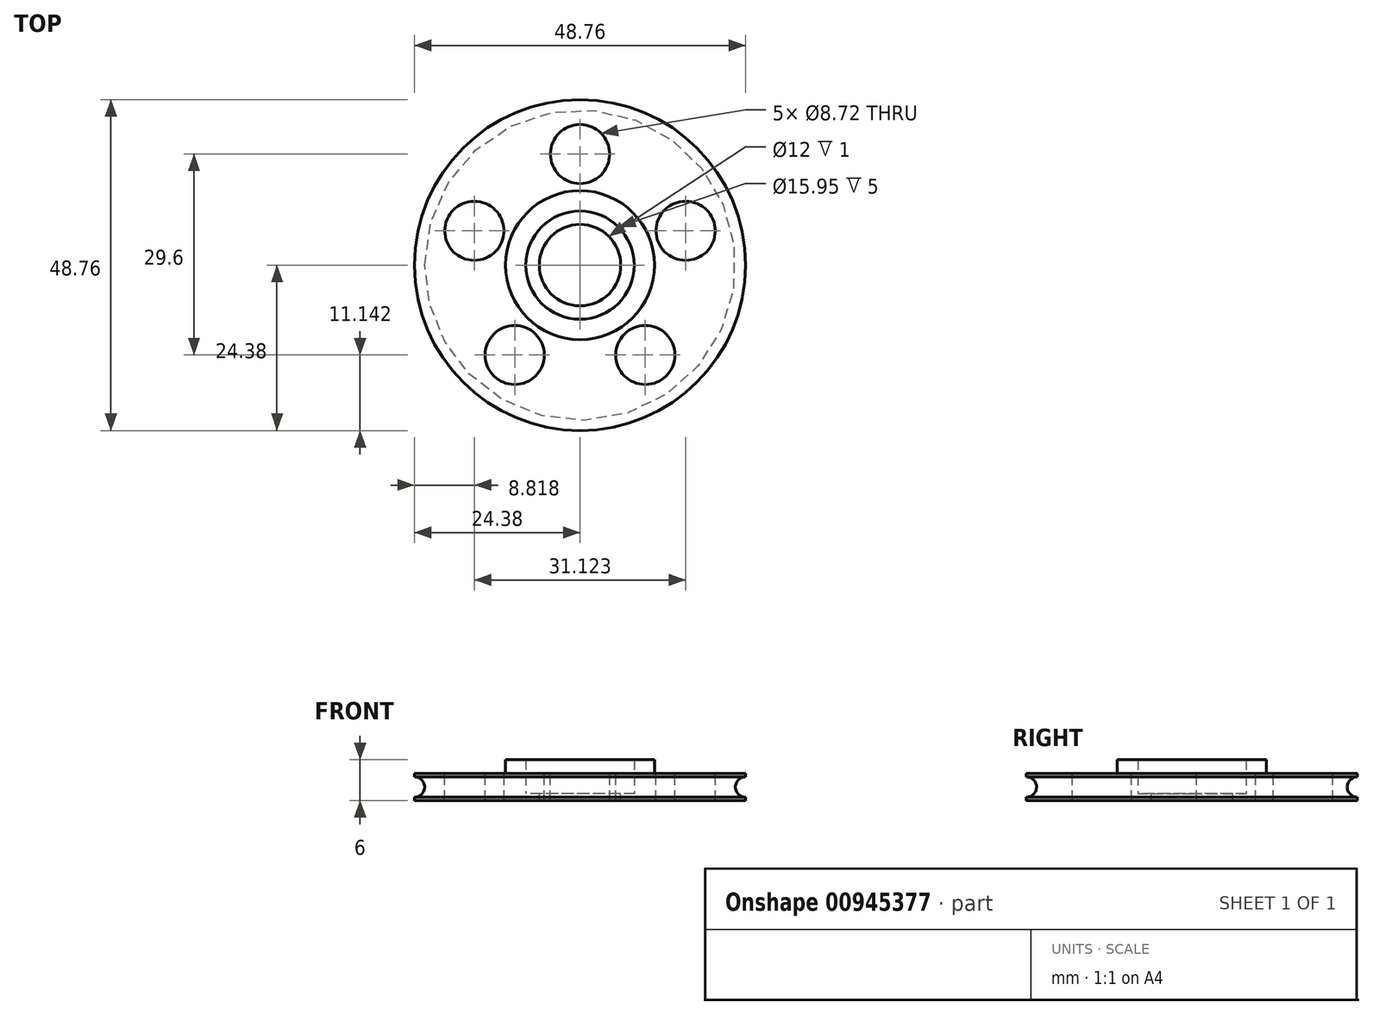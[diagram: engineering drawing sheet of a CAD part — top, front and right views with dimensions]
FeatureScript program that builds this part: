
annotation { "Feature Type Name" : "Feature", "Feature Type Description" : "" }
export const myFeature = defineFeature(function(context is Context, id is Id, definition is map)
    precondition{}
    {
        {
            var Q0;
            Q0=qCreatedBy(makeId("Top.planeOp"),FACE);
            var sketch = newSketch(context, id + "F0", { "sketchPlane" : qUnion([Q0])});
            skCircle(sketch, "E0", {"center": v(0, 0) * mm, "radius": 24.38 * mm});
            skSolve(sketch);
        }
        {
            var Q0;
            Q0=makeQuery(id+"F0.imprint","IMPRINT",FACE,{"disambiguationData":[TD([[makeQuery(id+"F0.imprint","IMPRINT",EDGE,{"derivedFrom":sQuery(id+"F0.wireOp",EDGE,"E0")}),1.0]])]});
            extrude(context, id + "F1", {"entities" : qUnion([Q0]), "depth" : 4 * mm, "offsetDistance" : 25.4 * mm});
        }
        {
            var Q0;
            Q0=makeQuery(id+"F1.opExtrude","CAP_FACE",FACE,{"disambiguationData":[OSD([sQuery(id+"F0.wireOp",EDGE,"E0"),sQuery(id+"F0.wireOp",EDGE,"n39IqKt5-bk1q-LU1x-fgod-8OyBNiFTd7FZ")])],"isStart":false});
            var sketch = newSketch(context, id + "F2", { "sketchPlane" : qUnion([Q0])});
            skCircle(sketch, "E1", {"center": v(0, 0) * mm, "radius": 7.97 * mm});
            skCircle(sketch, "E2.0", {"center": v(0, 0) * mm, "radius": 10.97 * mm});
            skSolve(sketch);
        }
        {
            var Q0;
            Q0=qSketchRegion(id+"F2",true);
            extrude(context, id + "F3", {"entities" : qUnion([Q0]), "operationType" : NewBodyOperationType.ADD, "depth" : 2 * mm, "offsetDistance" : 25.4 * mm});
        }
        {
            var Q0;
            Q0=makeQuery(id+"F3.boolean.opBoolean","SPLIT",FACE,{"disambiguationData":[TD([makeQuery(id+"F3.opExtrude","SWEPT_FACE",FACE,{"disambiguationData":[OSD([sQuery(id+"F2.wireOp",EDGE,"E1")])]})])],"derivedFrom":makeQuery(id+"F1.opExtrude","CAP_FACE",FACE,{"disambiguationData":[OSD([sQuery(id+"F0.wireOp",EDGE,"E0")])],"isStart":false})});
            var sketch = newSketch(context, id + "F4", { "sketchPlane" : qUnion([Q0])});
            skCircle(sketch, "E3", {"center": v(0, 0) * mm, "radius": 6 * mm});
            skSolve(sketch);
        }
        {
            var Q0;
            Q0=makeQuery(id+"F4.imprint","IMPRINT",FACE,{"disambiguationData":[TD([[makeQuery(id+"F4.imprint","IMPRINT",EDGE,{"derivedFrom":sQuery(id+"F4.wireOp",EDGE,"E3")}),1.0]])]});
            var Q1;
            Q1=makeQuery(id+"F4.imprint","IMPRINT",FACE,{"disambiguationData":[TD([[makeQuery(id+"F4.imprint","IMPRINT",EDGE,{"derivedFrom":makeQuery(id+"FgYK8jIepfClWtA_1.opExtrude","CAP_EDGE",EDGE,{"disambiguationData":[OSD([sQuery(id+"F8DXjnVyigKkjng_1.wireOp",EDGE,"EUjAMsCd-Zx2B-3j4q-cP5o-T3GrjTijNDqK")])],"isStart":false})}),1.0]])]});
            extrude(context, id + "F5", {"entities" : qUnion([Q0, Q1]), "operationType" : NewBodyOperationType.REMOVE, "oppositeDirection" : true, "depth" : 9 * mm, "offsetDistance" : 25.4 * mm});
        }
        {
            var Q0;
            Q0=qCreatedBy(makeId("Front.planeOp"),FACE);
            var sketch = newSketch(context, id + "F6", { "sketchPlane" : qUnion([Q0])});
            skCircle(sketch, "E4", {"center": v(-24.38, 2) * mm, "radius": 1.5 * mm});
            skLineSegment(sketch, "E5.bottom", {"start": v(-22.88, 0.65) * mm, "end": v(-25.02, 0.65) * mm});
            skLineSegment(sketch, "E5.top", {"start": v(-22.88, 3.35) * mm, "end": v(-25.02, 3.35) * mm});
            skLineSegment(sketch, "E5.left", {"start": v(-22.88, 0.65) * mm, "end": v(-22.88, 3.35) * mm});
            skLineSegment(sketch, "E5.right", {"start": v(-25.73, 1.35) * mm, "end": v(-25.73, 2.65) * mm});
            skLineSegment(sketch, "E6", {"start": v(0, 19.1) * mm, "end": v(0, -12.61) * mm, "construction": true});
            skLineSegment(sketch, "E7", {"start": v(-24.37, 3.35) * mm, "end": v(-22.88, 2) * mm});
            skLineSegment(sketch, "E8", {"start": v(-22.88, 2) * mm, "end": v(-24.38, 0.65) * mm});
            skLineSegment(sketch, "E9", {"start": v(-24.38, 0.65) * mm, "end": v(-24.37, 3.35) * mm});
            skSolve(sketch);
        }
        {
            var Q0;
            {var subQ0=sQuery(id+"F6.wireOp",EDGE,"E5.top");var subQ1=sQuery(id+"F6.wireOp",EDGE,"E4");var subQ2=makeQuery(id+"F6.imprint","INTERSECT",VERTEX,{"disambiguationData":[OD(0.0)],"derivedFrom":[subQ1,subQ0]});Q0=makeQuery(id+"F6.imprint","IMPRINT",FACE,{"disambiguationData":[TD([[makeQuery(id+"F6.imprint","IMPRINT",EDGE,{"disambiguationData":[TD([[subQ2,1.0]])],"derivedFrom":subQ1}),1.0]])]});}
            var Q1;
            {var subQ0=sQuery(id+"F6.wireOp",EDGE,"E5.bottom");var subQ1=sQuery(id+"F6.wireOp",EDGE,"E4");var subQ2=makeQuery(id+"F6.imprint","INTERSECT",VERTEX,{"disambiguationData":[OD(0.0)],"derivedFrom":[subQ1,subQ0]});Q1=makeQuery(id+"F6.imprint","IMPRINT",FACE,{"disambiguationData":[TD([[makeQuery(id+"F6.imprint","IMPRINT",EDGE,{"disambiguationData":[TD([[subQ2,-1.0]])],"derivedFrom":subQ1}),1.0]])]});}
            var Q2;
            {var subQ4=sQuery(id+"F6.wireOp",EDGE,"E5.right");Q2=makeQuery(id+"F6.imprint","IMPRINT",FACE,{"disambiguationData":[TD([[makeQuery(id+"F6.imprint","IMPRINT",EDGE,{"derivedFrom":subQ4}),-1.0]])]});}
            var Q3;
            {var subQ0=sQuery(id+"F6.wireOp",EDGE,"E7");Q3=makeQuery(id+"F6.imprint","IMPRINT",FACE,{"disambiguationData":[TD([[makeQuery(id+"F6.imprint","IMPRINT",EDGE,{"derivedFrom":subQ0}),1.0]])]});}
            var Q4;
            Q4=makeQuery(id+"F6.imprint","IMPRINT",FACE,{"disambiguationData":[TD([[makeQuery(id+"F6.imprint","IMPRINT",EDGE,{"derivedFrom":sQuery(id+"F6.wireOp",EDGE,"E7")}),-1.0]])]});
            var Q5;
            {var subQ0=sQuery(id+"F6.wireOp",EDGE,"E8");Q5=makeQuery(id+"F6.imprint","IMPRINT",FACE,{"disambiguationData":[TD([[makeQuery(id+"F6.imprint","IMPRINT",EDGE,{"derivedFrom":subQ0}),1.0]])]});}
            var Q6;
            Q6=sQuery(id+"F6.wireOp",EDGE,"E6");
            revolve(context, id + "F7", {"operationType" : NewBodyOperationType.REMOVE, "surfaceOperationType" : NewSurfaceOperationType.NEW, "entities" : qUnion([Q0, Q1, Q2, Q3, Q4, Q5]), "axis" : qUnion([Q6]), "revolveType" : RevolveType.FULL, "oppositeDirection" : true});
        }
        {
            var Q0;
            Q0=makeQuery(id+"F3.boolean.opBoolean","SPLIT",FACE,{"disambiguationData":[TD([makeQuery(id+"F3.opExtrude","SWEPT_FACE",FACE,{"disambiguationData":[OSD([sQuery(id+"F2.wireOp",EDGE,"E1")])]})])],"derivedFrom":makeQuery(id+"F1.opExtrude","CAP_FACE",FACE,{"disambiguationData":[OSD([sQuery(id+"F0.wireOp",EDGE,"E0")])],"isStart":false})});
            extrude(context, id + "F8", {"entities" : qUnion([Q0]), "operationType" : NewBodyOperationType.REMOVE, "oppositeDirection" : true, "depth" : 3 * mm, "offsetDistance" : 25 * mm});
        }
        {
            var Q0;
            {var subQ0=sQuery(id+"F0.wireOp",EDGE,"E0");Q0=makeQuery(id+"F3.boolean.opBoolean","SPLIT",FACE,{"disambiguationData":[TD([makeQuery(id+"F1.opExtrude","SWEPT_FACE",FACE,{"disambiguationData":[OSD([subQ0])]})])],"derivedFrom":makeQuery(id+"F1.opExtrude","CAP_FACE",FACE,{"disambiguationData":[OSD([subQ0])],"isStart":false})});}
            var sketch = newSketch(context, id + "F9", { "sketchPlane" : qUnion([Q0])});
            skCircle(sketch, "E10", {"center": v(0, 16.36) * mm, "radius": 4.36 * mm});
            skCircle(sketch, "E11.1.0", {"center": v(-15.56, 5.06) * mm, "radius": 4.36 * mm});
            skCircle(sketch, "E11.2.0", {"center": v(-9.62, -13.24) * mm, "radius": 4.36 * mm});
            skCircle(sketch, "E11.3.0", {"center": v(9.62, -13.24) * mm, "radius": 4.36 * mm});
            skCircle(sketch, "E11.4.0", {"center": v(15.56, 5.06) * mm, "radius": 4.36 * mm});
            skPoint(sketch, "E11.center", {"position": v(0, 0) * mm});
            skSolve(sketch);
        }
        {
            var Q0;
            Q0=qSketchRegion(id+"F9",true);
            extrude(context, id + "F10", {"entities" : qUnion([Q0]), "operationType" : NewBodyOperationType.REMOVE, "oppositeDirection" : true, "depth" : 25 * mm, "offsetDistance" : 25 * mm});
        }
    });
